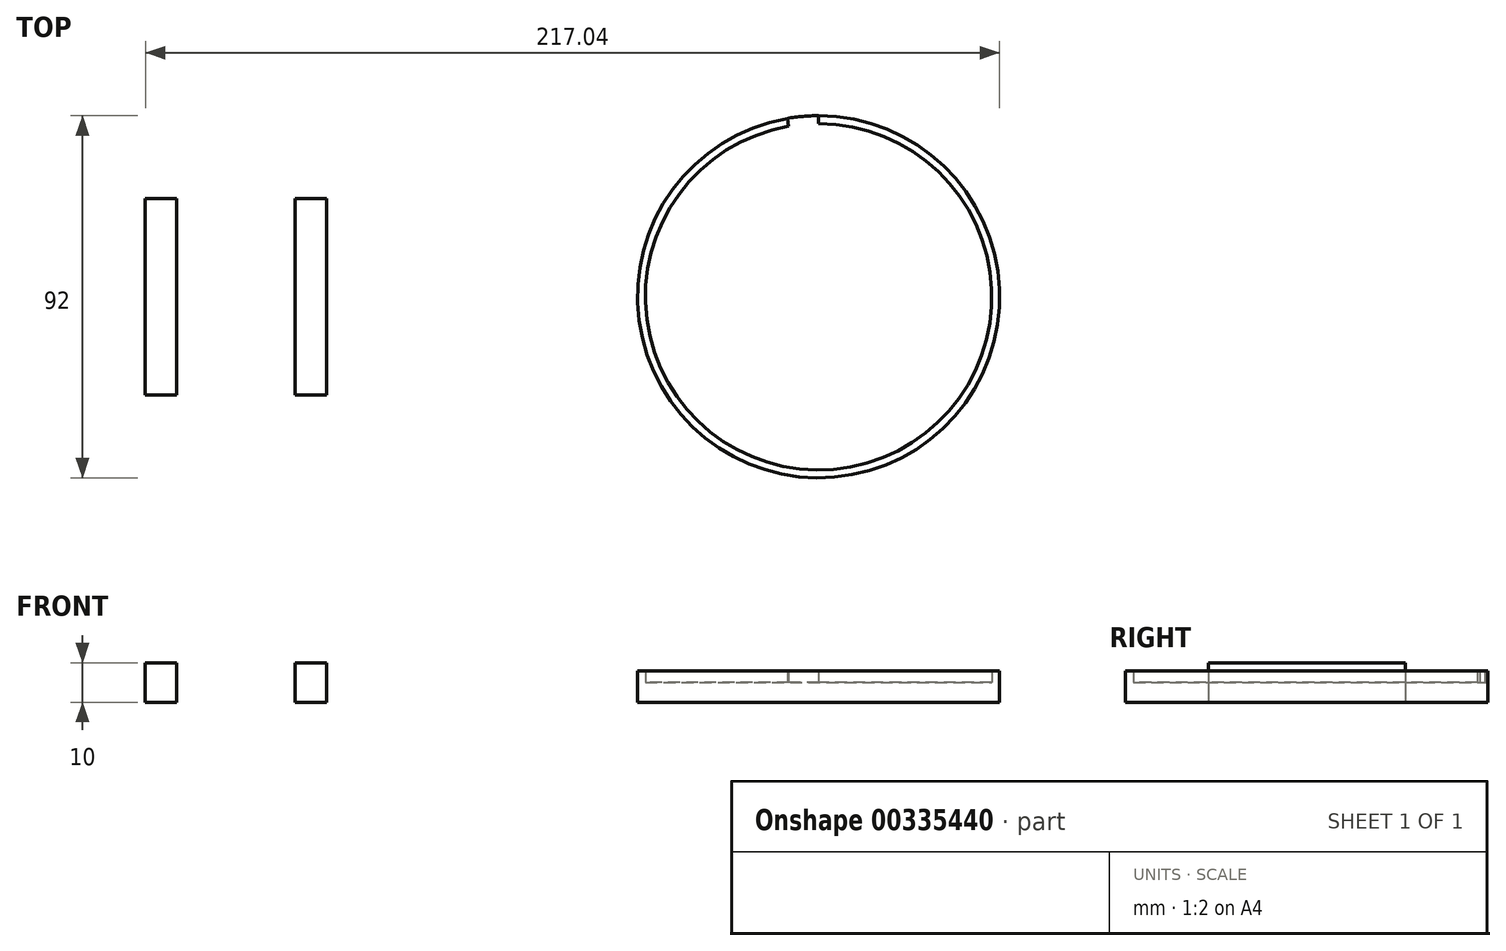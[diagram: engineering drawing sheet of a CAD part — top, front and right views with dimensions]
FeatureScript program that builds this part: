
annotation { "Feature Type Name" : "Feature", "Feature Type Description" : "" }
export const myFeature = defineFeature(function(context is Context, id is Id, definition is map)
    precondition{}
    {
        {
            var Q0;
            Q0=qCreatedBy(makeId("Top.planeOp"),FACE);
            var sketch = newSketch(context, id + "F0", { "sketchPlane" : qUnion([Q0])});
            skCircle(sketch, "E0", {"center": v(0, 0) * mm, "radius": 46 * mm});
            skSolve(sketch);
        }
        {
            var Q0;
            Q0=makeQuery(id+"F0.imprint","IMPRINT",FACE,{"disambiguationData":[TD([[makeQuery(id+"F0.imprint","IMPRINT",EDGE,{"derivedFrom":sQuery(id+"F0.wireOp",EDGE,"E0")}),1.0]])]});
            extrude(context, id + "F1", {"entities" : qUnion([Q0]), "depth" : 5 * mm});
        }
        {
            var Q0;
            Q0=makeQuery(id+"F1.opExtrude","CAP_FACE",FACE,{"disambiguationData":[OSD([sQuery(id+"F0.wireOp",EDGE,"E0")])],"isStart":false});
            var sketch = newSketch(context, id + "F2", { "sketchPlane" : qUnion([Q0])});
            skArc(sketch, "E1", {"start": v(0, 46) * mm, "mid": v(4, -45.83) * mm, "end": v(-7.97, 45.3) * mm});
            skArc(sketch, "E2", {"start": v(0, 44) * mm, "mid": v(3.83, -43.83) * mm, "end": v(-7.62, 43.33) * mm});
            skLineSegment(sketch, "E3", {"start": v(-7.62, 43.33) * mm, "end": v(-7.97, 45.3) * mm});
            skLineSegment(sketch, "E4", {"start": v(0, 44) * mm, "end": v(0, 46) * mm});
            skSolve(sketch);
        }
        {
            var Q0;
            Q0 = qSketchRegion(id + "F2", true);
            extrude(context, id + "F3", {"entities" : qUnion([Q0]), "operationType" : NewBodyOperationType.ADD, "depth" : 3 * mm});
        }
        {
            var Q0;
            Q0=qCreatedBy(makeId("Top.planeOp"),FACE);
            var sketch = newSketch(context, id + "F4", { "sketchPlane" : qUnion([Q0])});
            skLineSegment(sketch, "E5.bottom", {"start": v(-133.04, 25) * mm, "end": v(-125.04, 25) * mm});
            skLineSegment(sketch, "E5.top", {"start": v(-133.04, -25) * mm, "end": v(-125.04, -25) * mm});
            skLineSegment(sketch, "E5.left", {"start": v(-133.04, 25) * mm, "end": v(-133.04, -25) * mm});
            skLineSegment(sketch, "E5.right", {"start": v(-125.04, 25) * mm, "end": v(-125.04, -25) * mm});
            skLineSegment(sketch, "E6.bottom", {"start": v(-171.04, 25) * mm, "end": v(-163.04, 25) * mm});
            skLineSegment(sketch, "E6.top", {"start": v(-171.04, -25) * mm, "end": v(-163.04, -25) * mm});
            skLineSegment(sketch, "E6.left", {"start": v(-171.04, 25) * mm, "end": v(-171.04, -25) * mm});
            skLineSegment(sketch, "E6.right", {"start": v(-163.04, 25) * mm, "end": v(-163.04, -25) * mm});
            skSolve(sketch);
        }
        {
            var Q0;
            Q0 = qSketchRegion(id + "F4", true);
            extrude(context, id + "F5", {"entities" : qUnion([Q0]), "depth" : 10 * mm});
        }
    });
